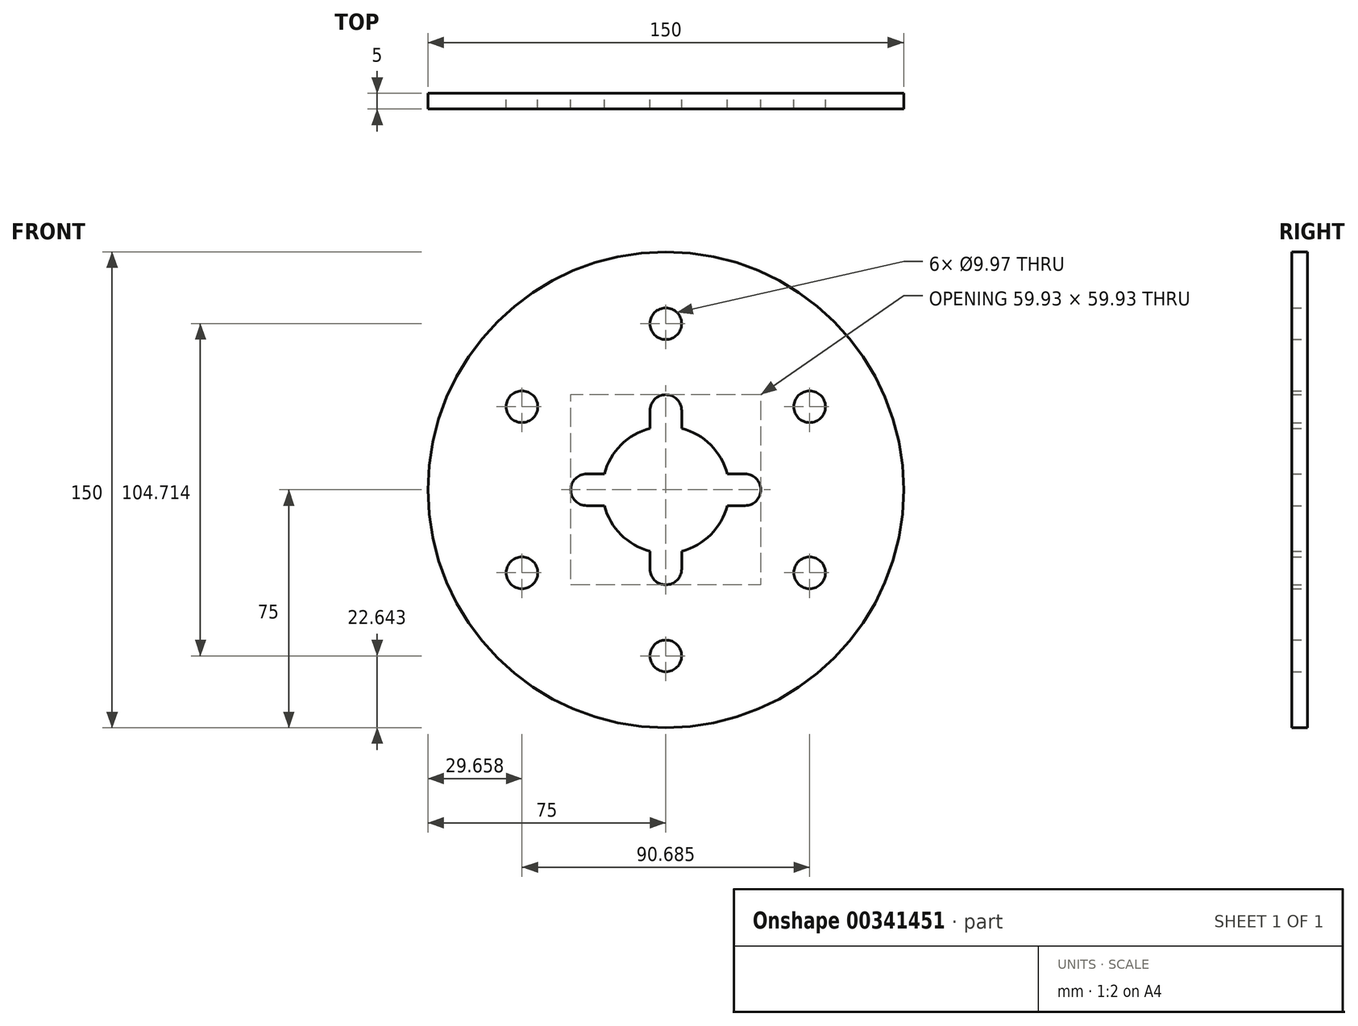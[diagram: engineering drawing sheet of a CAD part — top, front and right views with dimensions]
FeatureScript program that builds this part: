
annotation { "Feature Type Name" : "Feature", "Feature Type Description" : "" }
export const myFeature = defineFeature(function(context is Context, id is Id, definition is map)
    precondition{}
    {
        {
            var Q0;
            Q0=qCreatedBy(makeId("Front.planeOp"),FACE);
            var sketch = newSketch(context, id + "F0", { "sketchPlane" : qUnion([Q0])});
            skCircle(sketch, "E0", {"center": v(0, 0) * mm, "radius": 75 * mm});
            skArc(sketch, "E1", {"start": v(-4.99, 19.37) * mm, "mid": v(-14.14, 14.14) * mm, "end": v(-19.37, 4.99) * mm});
            skCircle(sketch, "E2", {"center": v(0, 0) * mm, "radius": 30 * mm, "construction": true});
            skLineSegment(sketch, "E3", {"start": v(4.99, 24.98) * mm, "end": v(4.99, 19.37) * mm});
            skLineSegment(sketch, "E4", {"start": v(-4.99, 24.98) * mm, "end": v(-4.99, 19.37) * mm});
            skCircle(sketch, "E5", {"center": v(0, 52.36) * mm, "radius": 4.99 * mm});
            skCircle(sketch, "E6.1.0", {"center": v(-45.34, 26.18) * mm, "radius": 4.99 * mm});
            skCircle(sketch, "E6.2.0", {"center": v(-45.34, -26.18) * mm, "radius": 4.99 * mm});
            skCircle(sketch, "E6.3.0", {"center": v(0, -52.36) * mm, "radius": 4.99 * mm});
            skCircle(sketch, "E6.4.0", {"center": v(45.34, -26.18) * mm, "radius": 4.99 * mm});
            skCircle(sketch, "E6.5.0", {"center": v(45.34, 26.18) * mm, "radius": 4.99 * mm});
            skCircle(sketch, "E7", {"center": v(0, 0) * mm, "radius": 52.36 * mm, "construction": true});
            skLineSegment(sketch, "E8", {"start": v(-24.98, 4.99) * mm, "end": v(-19.37, 4.99) * mm});
            skLineSegment(sketch, "E9", {"start": v(-24.98, -4.99) * mm, "end": v(-19.37, -4.99) * mm});
            skLineSegment(sketch, "E10", {"start": v(-4.99, -24.98) * mm, "end": v(-4.99, -19.37) * mm});
            skLineSegment(sketch, "E11", {"start": v(4.99, -24.98) * mm, "end": v(4.99, -19.37) * mm});
            skLineSegment(sketch, "E12", {"start": v(24.98, -4.99) * mm, "end": v(19.37, -4.99) * mm});
            skLineSegment(sketch, "E13", {"start": v(24.98, 4.99) * mm, "end": v(19.37, 4.99) * mm});
            skArc(sketch, "E14.trimOffspring", {"start": v(4.99, 24.98) * mm, "mid": v(0, 29.96) * mm, "end": v(-4.99, 24.98) * mm});
            skArc(sketch, "E15.trimOffspring", {"start": v(24.98, -4.99) * mm, "mid": v(29.96, 0) * mm, "end": v(24.98, 4.99) * mm});
            skArc(sketch, "E16.trimOffspring", {"start": v(19.37, 4.99) * mm, "mid": v(14.14, 14.14) * mm, "end": v(4.99, 19.37) * mm});
            skArc(sketch, "E17.trimOffspring", {"start": v(-4.99, -24.98) * mm, "mid": v(0, -29.96) * mm, "end": v(4.99, -24.98) * mm});
            skArc(sketch, "E18.trimOffspring", {"start": v(4.99, -19.37) * mm, "mid": v(14.14, -14.14) * mm, "end": v(19.37, -4.99) * mm});
            skArc(sketch, "E19.trimOffspring", {"start": v(-24.98, 4.99) * mm, "mid": v(-29.96, 0) * mm, "end": v(-24.98, -4.99) * mm});
            skArc(sketch, "E20.trimOffspring", {"start": v(-19.37, -4.99) * mm, "mid": v(-14.14, -14.14) * mm, "end": v(-4.99, -19.37) * mm});
            skSolve(sketch);
        }
        {
            var Q0;
            Q0 = qSketchRegion(id + "F0", true);
            extrude(context, id + "F1", {"entities" : qUnion([Q0]), "depth" : 5 * mm});
        }
    });
